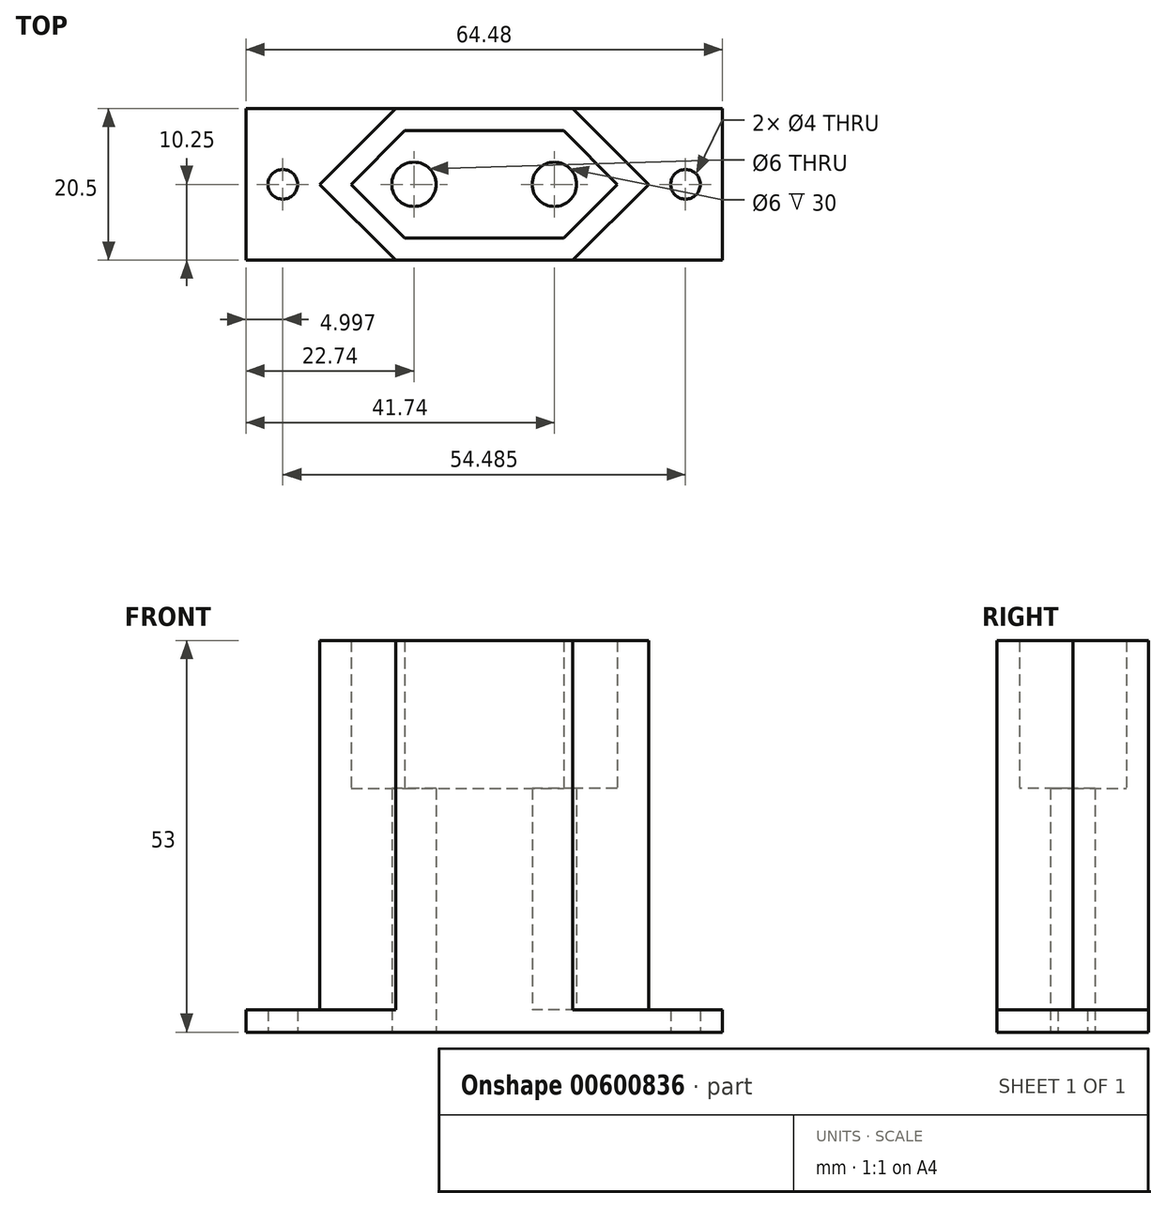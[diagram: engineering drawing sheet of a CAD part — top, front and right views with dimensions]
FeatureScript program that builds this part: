
annotation { "Feature Type Name" : "Feature", "Feature Type Description" : "" }
export const myFeature = defineFeature(function(context is Context, id is Id, definition is map)
    precondition{}
    {
        {
            var Q0;
            Q0=qCreatedBy(makeId("Top.planeOp"),FACE);
            var sketch = newSketch(context, id + "F0", { "sketchPlane" : qUnion([Q0])});
            skLineSegment(sketch, "E0.bottom", {"start": v(-10.75, 7.25) * mm, "end": v(10.75, 7.25) * mm});
            skLineSegment(sketch, "E0.top", {"start": v(-10.75, -7.25) * mm, "end": v(10.75, -7.25) * mm});
            skPoint(sketch, "E0.middle", {"position": v(0, 0) * mm});
            skLineSegment(sketch, "E1", {"start": v(-18, 0) * mm, "end": v(-10.75, 7.25) * mm});
            skLineSegment(sketch, "E2.MirrorCS", {"start": v(18, 0) * mm, "end": v(10.75, 7.25) * mm});
            skLineSegment(sketch, "E3.MirrorCS", {"start": v(-18, 0) * mm, "end": v(-10.75, -7.25) * mm});
            skLineSegment(sketch, "E4.MirrorCS", {"start": v(18, 0) * mm, "end": v(10.75, -7.25) * mm});
            skPoint(sketch, "E5.orphan", {"position": v(-18, 7.25) * mm});
            skPoint(sketch, "E6.orphan", {"position": v(18, 7.25) * mm});
            skPoint(sketch, "E7.orphan", {"position": v(18, -7.25) * mm});
            skPoint(sketch, "E0.left.end.orphan", {"position": v(-18, -7.25) * mm});
            skCircle(sketch, "E8", {"center": v(9.5, 0) * mm, "radius": 3 * mm});
            skCircle(sketch, "E9.MirrorC", {"center": v(-9.5, 0) * mm, "radius": 3 * mm});
            skLineSegment(sketch, "E10.0", {"start": v(-22.24, 0) * mm, "end": v(-12, 10.25) * mm});
            skLineSegment(sketch, "E10.1", {"start": v(22.24, 0) * mm, "end": v(12, 10.25) * mm});
            skLineSegment(sketch, "E10.2", {"start": v(22.24, 0) * mm, "end": v(12, -10.25) * mm});
            skLineSegment(sketch, "E10.3", {"start": v(-12, 10.25) * mm, "end": v(12, 10.25) * mm});
            skLineSegment(sketch, "E10.4", {"start": v(-12, -10.25) * mm, "end": v(12, -10.25) * mm});
            skLineSegment(sketch, "E10.5", {"start": v(-22.24, 0) * mm, "end": v(-12, -10.25) * mm});
            skLineSegment(sketch, "E11.bottom", {"start": v(-32.24, 10.25) * mm, "end": v(32.24, 10.25) * mm});
            skLineSegment(sketch, "E11.top", {"start": v(-32.24, -10.25) * mm, "end": v(32.24, -10.25) * mm});
            skLineSegment(sketch, "E11.left", {"start": v(-32.24, 10.25) * mm, "end": v(-32.24, -10.25) * mm});
            skLineSegment(sketch, "E11.right", {"start": v(32.24, 10.25) * mm, "end": v(32.24, -10.25) * mm});
            skCircle(sketch, "E12", {"center": v(27.24, 0) * mm, "radius": 2 * mm});
            skCircle(sketch, "E13.MirrorC", {"center": v(-27.24, 0) * mm, "radius": 2 * mm});
            skSolve(sketch);
        }
        {
            var Q0;
            Q0=makeQuery(id+"F0.imprint","IMPRINT",FACE,{"disambiguationData":[TD([[makeQuery(id+"F0.imprint","IMPRINT",EDGE,{"derivedFrom":sQuery(id+"F0.wireOp",EDGE,"E0.bottom")}),1.0]])]});
            var Q1;
            Q1=makeQuery(id+"F0.imprint","IMPRINT",FACE,{"disambiguationData":[TD([[makeQuery(id+"F0.imprint","IMPRINT",EDGE,{"derivedFrom":sQuery(id+"F0.wireOp",EDGE,"E9.MirrorC")}),-1.0]])]});
            var Q2;
            Q2=makeQuery(id+"F0.imprint","IMPRINT",FACE,{"disambiguationData":[TD([[makeQuery(id+"F0.imprint","IMPRINT",EDGE,{"derivedFrom":sQuery(id+"F0.wireOp",EDGE,"E0.bottom")}),-1.0]])]});
            var Q3;
            {var subQ4=sQuery(id+"F0.wireOp",EDGE,"E10.1");Q3=makeQuery(id+"F0.imprint","IMPRINT",FACE,{"disambiguationData":[TD([[makeQuery(id+"F0.imprint","IMPRINT",EDGE,{"derivedFrom":subQ4}),-1.0]])]});}
            var Q4;
            Q4=makeQuery(id+"F0.imprint","IMPRINT",FACE,{"disambiguationData":[TD([[makeQuery(id+"F0.imprint","IMPRINT",EDGE,{"derivedFrom":sQuery(id+"F0.wireOp",EDGE,"E8")}),1.0]])]});
            var Q5;
            {var subQ4=sQuery(id+"F0.wireOp",EDGE,"E10.0");Q5=makeQuery(id+"F0.imprint","IMPRINT",FACE,{"disambiguationData":[TD([[makeQuery(id+"F0.imprint","IMPRINT",EDGE,{"derivedFrom":subQ4}),1.0]])]});}
            extrude(context, id + "F1", {"entities" : qUnion([Q0, Q1, Q2, Q3, Q4, Q5]), "depth" : 3 * mm, "offsetDistance" : 25 * mm});
        }
        {
            var Q0;
            Q0=makeQuery(id+"F0.imprint","IMPRINT",FACE,{"disambiguationData":[TD([[makeQuery(id+"F0.imprint","IMPRINT",EDGE,{"derivedFrom":sQuery(id+"F0.wireOp",EDGE,"E0.bottom")}),1.0]])]});
            extrude(context, id + "F2", {"entities" : qUnion([Q0]), "operationType" : NewBodyOperationType.ADD, "depth" : 53 * mm, "offsetDistance" : 25 * mm});
        }
        {
            var Q0;
            Q0=makeQuery(id+"F0.imprint","IMPRINT",FACE,{"disambiguationData":[TD([[makeQuery(id+"F0.imprint","IMPRINT",EDGE,{"derivedFrom":sQuery(id+"F0.wireOp",EDGE,"E0.bottom")}),-1.0]])]});
            extrude(context, id + "F3", {"entities" : qUnion([Q0]), "operationType" : NewBodyOperationType.ADD, "depth" : 33 * mm, "offsetDistance" : 25 * mm});
        }
    });
